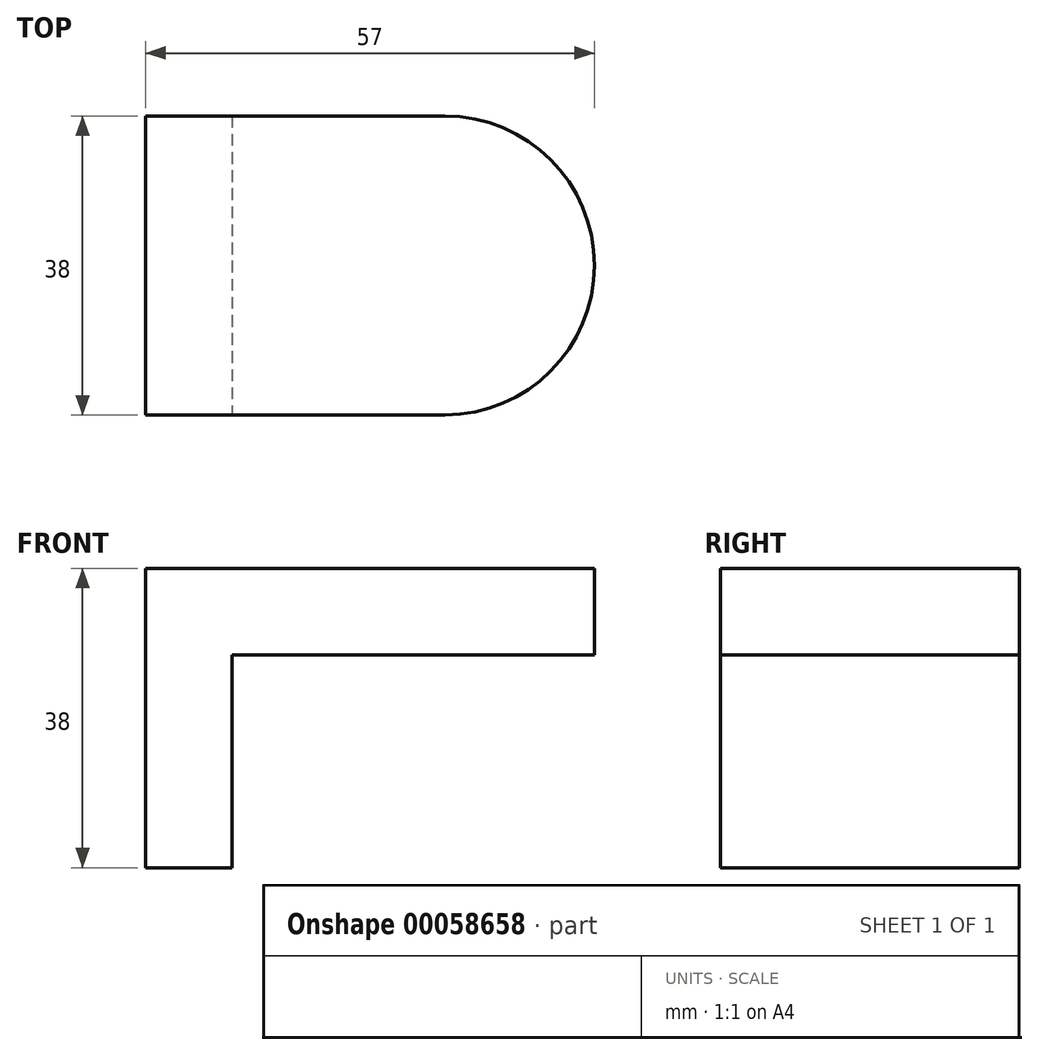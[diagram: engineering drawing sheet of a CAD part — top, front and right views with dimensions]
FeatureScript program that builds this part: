
annotation { "Feature Type Name" : "Feature", "Feature Type Description" : "" }
export const myFeature = defineFeature(function(context is Context, id is Id, definition is map)
    precondition{}
    {
        {
            var Q0;
            Q0=qCreatedBy(makeId("Top.planeOp"),FACE);
            var sketch = newSketch(context, id + "F0", { "sketchPlane" : qUnion([Q0])});
            skLineSegment(sketch, "E0.bottom", {"start": v(-37.2, 19.44) * mm, "end": v(0.8, 19.44) * mm});
            skLineSegment(sketch, "E0.top", {"start": v(-37.2, -18.56) * mm, "end": v(0.8, -18.56) * mm});
            skLineSegment(sketch, "E0.left", {"start": v(-37.2, 19.44) * mm, "end": v(-37.2, -18.56) * mm});
            skLineSegment(sketch, "E0.right", {"start": v(0.8, 19.44) * mm, "end": v(0.8, -18.56) * mm});
            skArc(sketch, "E1", {"start": v(0.8, -18.56) * mm, "mid": v(19.8, 0.44) * mm, "end": v(0.8, 19.44) * mm});
            skSolve(sketch);
        }
        {
            var Q0;
            Q0=makeQuery(id+"F0.imprint","IMPRINT",FACE,{"disambiguationData":[TD([[makeQuery(id+"F0.imprint","IMPRINT",EDGE,{"derivedFrom":sQuery(id+"F0.wireOp",EDGE,"E0.bottom")}),-1.0]])]});
            var Q1;
            Q1=makeQuery(id+"F0.imprint","IMPRINT",FACE,{"disambiguationData":[TD([[makeQuery(id+"F0.imprint","IMPRINT",EDGE,{"derivedFrom":sQuery(id+"F0.wireOp",EDGE,"E0.right")}),1.0]])]});
            extrude(context, id + "F1", {"entities" : qUnion([Q0, Q1]), "oppositeDirection" : true, "depth" : 11 * mm});
        }
        {
            var Q0;
            Q0=makeQuery(id+"F1.opExtrude","CAP_FACE",FACE,{"disambiguationData":[OSD([sQuery(id+"F0.wireOp",EDGE,"E0.bottom"),sQuery(id+"F0.wireOp",EDGE,"E0.top"),sQuery(id+"F0.wireOp",EDGE,"E0.left"),sQuery(id+"F0.wireOp",EDGE,"E1")])],"isStart":false});
            var sketch = newSketch(context, id + "F2", { "sketchPlane" : qUnion([Q0])});
            skLineSegment(sketch, "E2", {"start": v(-26.2, -19.44) * mm, "end": v(-26.2, 18.56) * mm});
            skSolve(sketch);
        }
        {
            var Q0;
            Q0 = qSketchRegion(id + "F2", true);
            var Q1;
            {var subQ0=sQuery(id+"F2.wireOp",EDGE,"E2");Q1=makeQuery(id+"F2.imprint","IMPRINT",FACE,{"disambiguationData":[TD([[makeQuery(id+"F2.imprint","IMPRINT",EDGE,{"derivedFrom":subQ0}),1.0]])]});}
            extrude(context, id + "F3", {"entities" : qUnion([Q0, Q1]), "operationType" : NewBodyOperationType.ADD, "depth" : 27 * mm});
        }
    });
